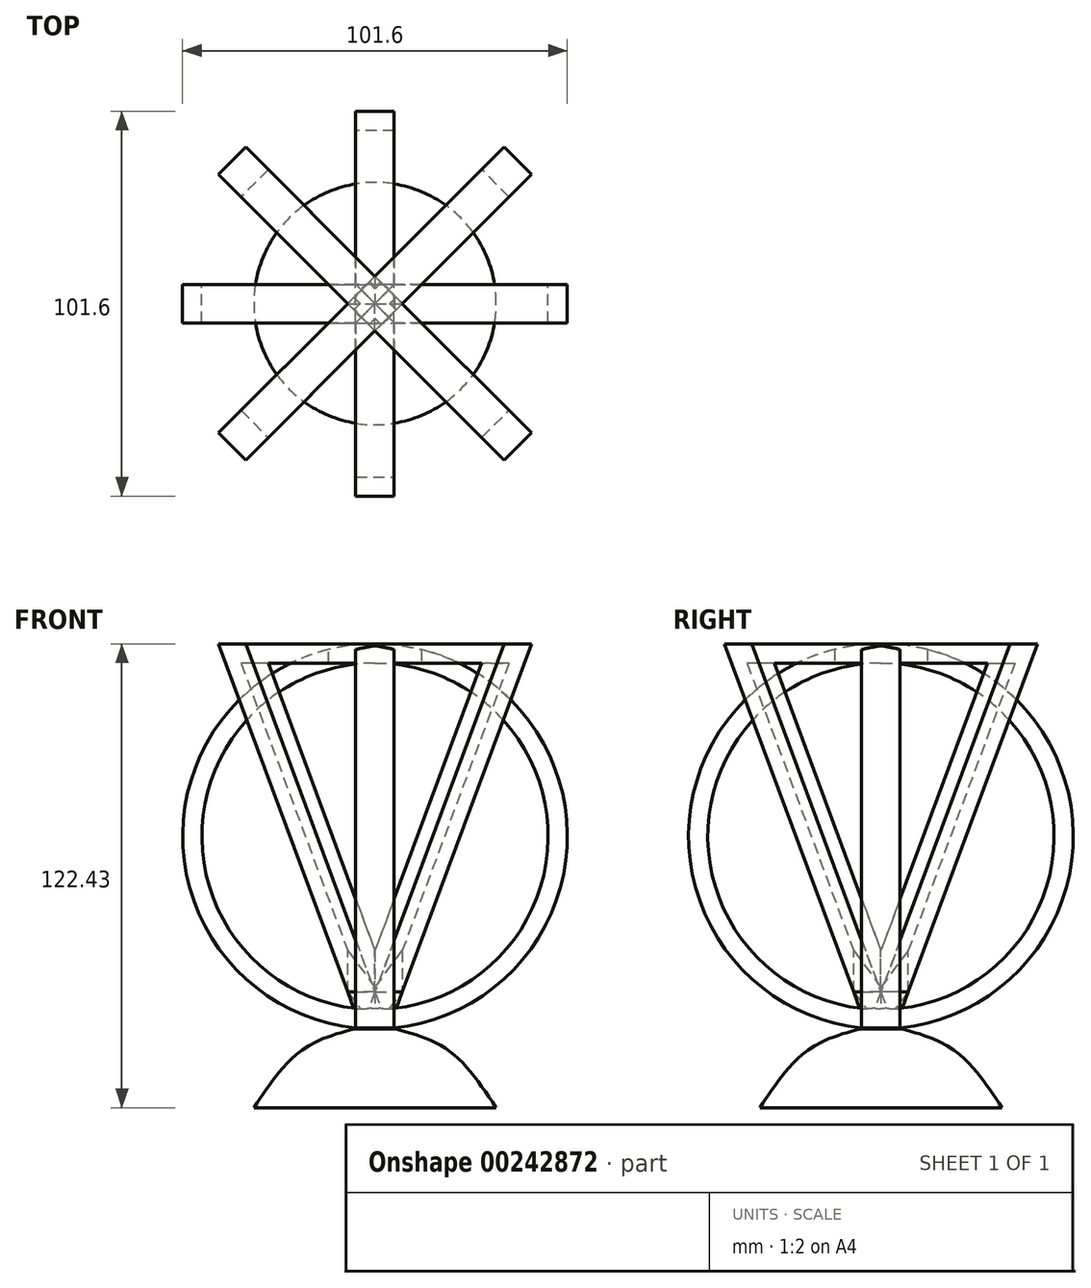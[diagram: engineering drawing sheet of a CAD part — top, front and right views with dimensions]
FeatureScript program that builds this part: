
annotation { "Feature Type Name" : "Feature", "Feature Type Description" : "" }
export const myFeature = defineFeature(function(context is Context, id is Id, definition is map)
    precondition{}
    {
        {
            var Q0;
            Q0=qCreatedBy(makeId("Front.planeOp"),FACE);
            var sketch = newSketch(context, id + "F0", { "sketchPlane" : qUnion([Q0])});
            skCircle(sketch, "E0", {"center": v(0, 0) * mm, "radius": 45.72 * mm});
            skCircle(sketch, "E1", {"center": v(0, 0) * mm, "radius": 50.8 * mm});
            skLineSegment(sketch, "E2", {"start": v(0, 45.72) * mm, "end": v(0, 50.8) * mm});
            skLineSegment(sketch, "E3", {"start": v(0, -50.8) * mm, "end": v(0, -45.72) * mm});
            skLineSegment(sketch, "E4", {"start": v(0, -50.8) * mm, "end": v(0, 45.72) * mm});
            skSolve(sketch);
        }
        {
            var Q0;
            {var subQ0=sQuery(id+"F0.wireOp",EDGE,"E2");Q0=makeQuery(id+"F0.imprint","IMPRINT",FACE,{"disambiguationData":[TD([[makeQuery(id+"F0.imprint","IMPRINT",EDGE,{"derivedFrom":subQ0}),-1.0]])]});}
            extrude(context, id + "F1", {"entities" : qUnion([Q0]), "depth" : 5.08 * mm});
        }
        {
            var Q0;
            {var subQ1=sQuery(id+"F0.wireOp",EDGE,"E2");Q0=makeQuery(id+"F0.imprint","IMPRINT",FACE,{"disambiguationData":[TD([[makeQuery(id+"F0.imprint","IMPRINT",EDGE,{"derivedFrom":subQ1}),-1.0]])]});}
            extrude(context, id + "F2", {"entities" : qUnion([Q0]), "operationType" : NewBodyOperationType.ADD, "oppositeDirection" : true, "depth" : 5.08 * mm});
        }
        {
            var Q0;
            Q0=makeQuery(id+"F1.opExtrude","SWEPT_BODY",BODY,{"disambiguationData":[OSD([sQuery(id+"F0.wireOp",EDGE,"E0"),sQuery(id+"F0.wireOp",EDGE,"E1"),sQuery(id+"F0.wireOp",EDGE,"E2"),sQuery(id+"F0.wireOp",EDGE,"E4")])]});
            var Q1;
            Q1=sQuery(id+"F0.wireOp",EDGE,"E4");
            circularPattern(context, id + "F3", {"entities" : qUnion([Q0]), "axis" : qUnion([Q1]), "angle" : 360 * degree, "instanceCount" : 4, "equalSpace" : true});
        }
        {
            var Q0;
            Q0=qCreatedBy(makeId("Front.planeOp"),FACE);
            var Q1;
            Q1=sQuery(id+"F0.wireOp",EDGE,"E4");
            cPlane(context, id + "F4", {"entities" : qUnion([Q0, Q1]), "cplaneType" : CPlaneType.LINE_ANGLE, "offset" : 25.4 * mm, "angle" : 45 * degree, "width" : 152.4 * mm, "height" : 152.4 * mm});
        }
        {
            var Q0;
            Q0=qCreatedBy(id+"F4.planeOp",FACE);
            var sketch = newSketch(context, id + "F5", { "sketchPlane" : qUnion([Q0])});
            skPoint(sketch, "E5.0", {"position": v(0, 50.8) * mm});
            skPoint(sketch, "E6.0", {"position": v(0, -50.8) * mm});
            skLineSegment(sketch, "E7", {"start": v(0, 50.8) * mm, "end": v(-53.34, 50.8) * mm});
            skLineSegment(sketch, "E8", {"start": v(-53.34, 50.8) * mm, "end": v(0, -50.8) * mm});
            skLineSegment(sketch, "E9.0", {"start": v(-44.94, 45.72) * mm, "end": v(3.96, -47.41) * mm});
            skLineSegment(sketch, "E9.1", {"start": v(0, 45.72) * mm, "end": v(-44.94, 45.72) * mm});
            skLineSegment(sketch, "E10", {"start": v(0, 45.72) * mm, "end": v(0, 50.8) * mm});
            skLineSegment(sketch, "E11", {"start": v(0, -50.8) * mm, "end": v(0, -39.87) * mm});
            skSolve(sketch);
        }
        {
            var Q0;
            Q0 = qSketchRegion(id + "F5", true);
            extrude(context, id + "F6", {"entities" : qUnion([Q0]), "depth" : 5.08 * mm});
        }
        {
            var Q0;
            Q0=makeQuery(id+"F6.opExtrude","CAP_FACE",FACE,{"disambiguationData":[OSD([sQuery(id+"F5.wireOp",EDGE,"E7"),sQuery(id+"F5.wireOp",EDGE,"E8"),sQuery(id+"F5.wireOp",EDGE,"E9.0"),sQuery(id+"F5.wireOp",EDGE,"E9.1"),sQuery(id+"F5.wireOp",EDGE,"E10"),sQuery(id+"F5.wireOp",EDGE,"E11")])],"isStart":true});
            extrude(context, id + "F7", {"entities" : qUnion([Q0]), "depth" : 5.08 * mm});
        }
        {
            var Q0;
            Q0=makeQuery(id+"F7.opExtrude","SWEPT_BODY",BODY,{"disambiguationData":[OSD([sQuery(id+"F5.wireOp",EDGE,"E7"),sQuery(id+"F5.wireOp",EDGE,"E8"),sQuery(id+"F5.wireOp",EDGE,"E9.0"),sQuery(id+"F5.wireOp",EDGE,"E9.1"),sQuery(id+"F5.wireOp",EDGE,"E10"),sQuery(id+"F5.wireOp",EDGE,"E11")])]});
            var Q1;
            Q1=makeQuery(id+"F6.opExtrude","SWEPT_BODY",BODY,{"disambiguationData":[OSD([sQuery(id+"F5.wireOp",EDGE,"E7"),sQuery(id+"F5.wireOp",EDGE,"E8"),sQuery(id+"F5.wireOp",EDGE,"E9.0"),sQuery(id+"F5.wireOp",EDGE,"E9.1"),sQuery(id+"F5.wireOp",EDGE,"E10"),sQuery(id+"F5.wireOp",EDGE,"E11")])]});
            var Q2;
            Q2=sQuery(id+"F0.wireOp",EDGE,"E4");
            circularPattern(context, id + "F8", {"entities" : qUnion([Q0, Q1]), "axis" : qUnion([Q2]), "angle" : 360 * degree, "instanceCount" : 4, "equalSpace" : true});
        }
        {
            var Q0;
            Q0=qCreatedBy(makeId("Front.planeOp"),FACE);
            var sketch = newSketch(context, id + "F9", { "sketchPlane" : qUnion([Q0])});
            skPoint(sketch, "E12.0", {"position": v(0, -50.8) * mm});
            skLineSegment(sketch, "E13", {"start": v(0, -50.8) * mm, "end": v(0, -71.63) * mm});
            skLineSegment(sketch, "E14", {"start": v(0, -71.63) * mm, "end": v(31.99, -71.63) * mm});
            skLineSegment(sketch, "E15", {"start": v(0, -50.8) * mm, "end": v(5.36, -50.8) * mm});
            skFitSpline(sketch, "E16", {"points": [v(5.36, -50.8) * mm, v(19.55, -56.63) * mm, v(31.99, -71.63) * mm], "startDerivative": vector(31.76, -8.66) * mm, "endDerivative": vector(21.7, -32.51) * mm});
            skSolve(sketch);
        }
        {
            var Q0;
            Q0=makeQuery(id+"F9.imprint","IMPRINT",FACE,{"disambiguationData":[TD([[makeQuery(id+"F9.imprint","IMPRINT",EDGE,{"derivedFrom":sQuery(id+"F9.wireOp",EDGE,"E13")}),1.0]])]});
            var Q1;
            Q1=sQuery(id+"F9.wireOp",EDGE,"E13");
            revolve(context, id + "F10", {"entities" : qUnion([Q0]), "axis" : qUnion([Q1]), "revolveType" : RevolveType.FULL});
        }
        {
            var Q0;
            Q0=makeQuery(id+"F3.opPattern","COPY",BODY,{"derivedFrom":makeQuery(id+"F1.opExtrude","SWEPT_BODY",BODY,{"disambiguationData":[OSD([sQuery(id+"F0.wireOp",EDGE,"E0"),sQuery(id+"F0.wireOp",EDGE,"E1"),sQuery(id+"F0.wireOp",EDGE,"E2"),sQuery(id+"F0.wireOp",EDGE,"E4")])]}),"instanceName":"1"});
            var Q1;
            Q1=makeQuery(id+"F8.opPattern","COPY",BODY,{"derivedFrom":makeQuery(id+"F7.opExtrude","SWEPT_BODY",BODY,{"disambiguationData":[OSD([sQuery(id+"F5.wireOp",EDGE,"E7"),sQuery(id+"F5.wireOp",EDGE,"E8"),sQuery(id+"F5.wireOp",EDGE,"E9.0"),sQuery(id+"F5.wireOp",EDGE,"E9.1"),sQuery(id+"F5.wireOp",EDGE,"E10"),sQuery(id+"F5.wireOp",EDGE,"E11")])]}),"instanceName":"1"});
            var Q2;
            Q2=makeQuery(id+"F8.opPattern","COPY",BODY,{"derivedFrom":makeQuery(id+"F6.opExtrude","SWEPT_BODY",BODY,{"disambiguationData":[OSD([sQuery(id+"F5.wireOp",EDGE,"E7"),sQuery(id+"F5.wireOp",EDGE,"E8"),sQuery(id+"F5.wireOp",EDGE,"E9.0"),sQuery(id+"F5.wireOp",EDGE,"E9.1"),sQuery(id+"F5.wireOp",EDGE,"E10"),sQuery(id+"F5.wireOp",EDGE,"E11")])]}),"instanceName":"1"});
            var Q3;
            Q3=makeQuery(id+"F8.opPattern","COPY",BODY,{"derivedFrom":makeQuery(id+"F7.opExtrude","SWEPT_BODY",BODY,{"disambiguationData":[OSD([sQuery(id+"F5.wireOp",EDGE,"E7"),sQuery(id+"F5.wireOp",EDGE,"E8"),sQuery(id+"F5.wireOp",EDGE,"E9.0"),sQuery(id+"F5.wireOp",EDGE,"E9.1"),sQuery(id+"F5.wireOp",EDGE,"E10"),sQuery(id+"F5.wireOp",EDGE,"E11")])]}),"instanceName":"2"});
            var Q4;
            Q4=makeQuery(id+"F8.opPattern","COPY",BODY,{"derivedFrom":makeQuery(id+"F6.opExtrude","SWEPT_BODY",BODY,{"disambiguationData":[OSD([sQuery(id+"F5.wireOp",EDGE,"E7"),sQuery(id+"F5.wireOp",EDGE,"E8"),sQuery(id+"F5.wireOp",EDGE,"E9.0"),sQuery(id+"F5.wireOp",EDGE,"E9.1"),sQuery(id+"F5.wireOp",EDGE,"E10"),sQuery(id+"F5.wireOp",EDGE,"E11")])]}),"instanceName":"2"});
            var Q5;
            Q5=makeQuery(id+"F3.opPattern","COPY",BODY,{"derivedFrom":makeQuery(id+"F1.opExtrude","SWEPT_BODY",BODY,{"disambiguationData":[OSD([sQuery(id+"F0.wireOp",EDGE,"E0"),sQuery(id+"F0.wireOp",EDGE,"E1"),sQuery(id+"F0.wireOp",EDGE,"E2"),sQuery(id+"F0.wireOp",EDGE,"E4")])]}),"instanceName":"3"});
            var Q6;
            Q6=makeQuery(id+"F8.opPattern","COPY",BODY,{"derivedFrom":makeQuery(id+"F7.opExtrude","SWEPT_BODY",BODY,{"disambiguationData":[OSD([sQuery(id+"F5.wireOp",EDGE,"E7"),sQuery(id+"F5.wireOp",EDGE,"E8"),sQuery(id+"F5.wireOp",EDGE,"E9.0"),sQuery(id+"F5.wireOp",EDGE,"E9.1"),sQuery(id+"F5.wireOp",EDGE,"E10"),sQuery(id+"F5.wireOp",EDGE,"E11")])]}),"instanceName":"3"});
            var Q7;
            Q7=makeQuery(id+"F10.opRevolve","SWEPT_BODY",BODY,{"disambiguationData":[OSD([sQuery(id+"F9.wireOp",EDGE,"E13"),sQuery(id+"F9.wireOp",EDGE,"E14"),sQuery(id+"F9.wireOp",EDGE,"E15"),sQuery(id+"F9.wireOp",EDGE,"E16")])]});
            var Q8;
            Q8=makeQuery(id+"F1.opExtrude","SWEPT_BODY",BODY,{"disambiguationData":[OSD([sQuery(id+"F0.wireOp",EDGE,"E0"),sQuery(id+"F0.wireOp",EDGE,"E1"),sQuery(id+"F0.wireOp",EDGE,"E2"),sQuery(id+"F0.wireOp",EDGE,"E4")])]});
            var Q9;
            Q9=makeQuery(id+"F7.opExtrude","SWEPT_BODY",BODY,{"disambiguationData":[OSD([sQuery(id+"F5.wireOp",EDGE,"E7"),sQuery(id+"F5.wireOp",EDGE,"E8"),sQuery(id+"F5.wireOp",EDGE,"E9.0"),sQuery(id+"F5.wireOp",EDGE,"E9.1"),sQuery(id+"F5.wireOp",EDGE,"E10"),sQuery(id+"F5.wireOp",EDGE,"E11")])]});
            var Q10;
            Q10=makeQuery(id+"F6.opExtrude","SWEPT_BODY",BODY,{"disambiguationData":[OSD([sQuery(id+"F5.wireOp",EDGE,"E7"),sQuery(id+"F5.wireOp",EDGE,"E8"),sQuery(id+"F5.wireOp",EDGE,"E9.0"),sQuery(id+"F5.wireOp",EDGE,"E9.1"),sQuery(id+"F5.wireOp",EDGE,"E10"),sQuery(id+"F5.wireOp",EDGE,"E11")])]});
            var Q11;
            Q11=makeQuery(id+"F8.opPattern","COPY",BODY,{"derivedFrom":makeQuery(id+"F6.opExtrude","SWEPT_BODY",BODY,{"disambiguationData":[OSD([sQuery(id+"F5.wireOp",EDGE,"E7"),sQuery(id+"F5.wireOp",EDGE,"E8"),sQuery(id+"F5.wireOp",EDGE,"E9.0"),sQuery(id+"F5.wireOp",EDGE,"E9.1"),sQuery(id+"F5.wireOp",EDGE,"E10"),sQuery(id+"F5.wireOp",EDGE,"E11")])]}),"instanceName":"3"});
            var Q12;
            Q12=makeQuery(id+"F3.opPattern","COPY",BODY,{"derivedFrom":makeQuery(id+"F1.opExtrude","SWEPT_BODY",BODY,{"disambiguationData":[OSD([sQuery(id+"F0.wireOp",EDGE,"E0"),sQuery(id+"F0.wireOp",EDGE,"E1"),sQuery(id+"F0.wireOp",EDGE,"E2"),sQuery(id+"F0.wireOp",EDGE,"E4")])]}),"instanceName":"2"});
            booleanBodies(context, id + "F11", {"operationType" : BooleanOperationType.UNION, "tools" : qUnion([Q0, Q1, Q2, Q3, Q4, Q5, Q6, Q7, Q8, Q9, Q10, Q11, Q12])});
        }
    });
